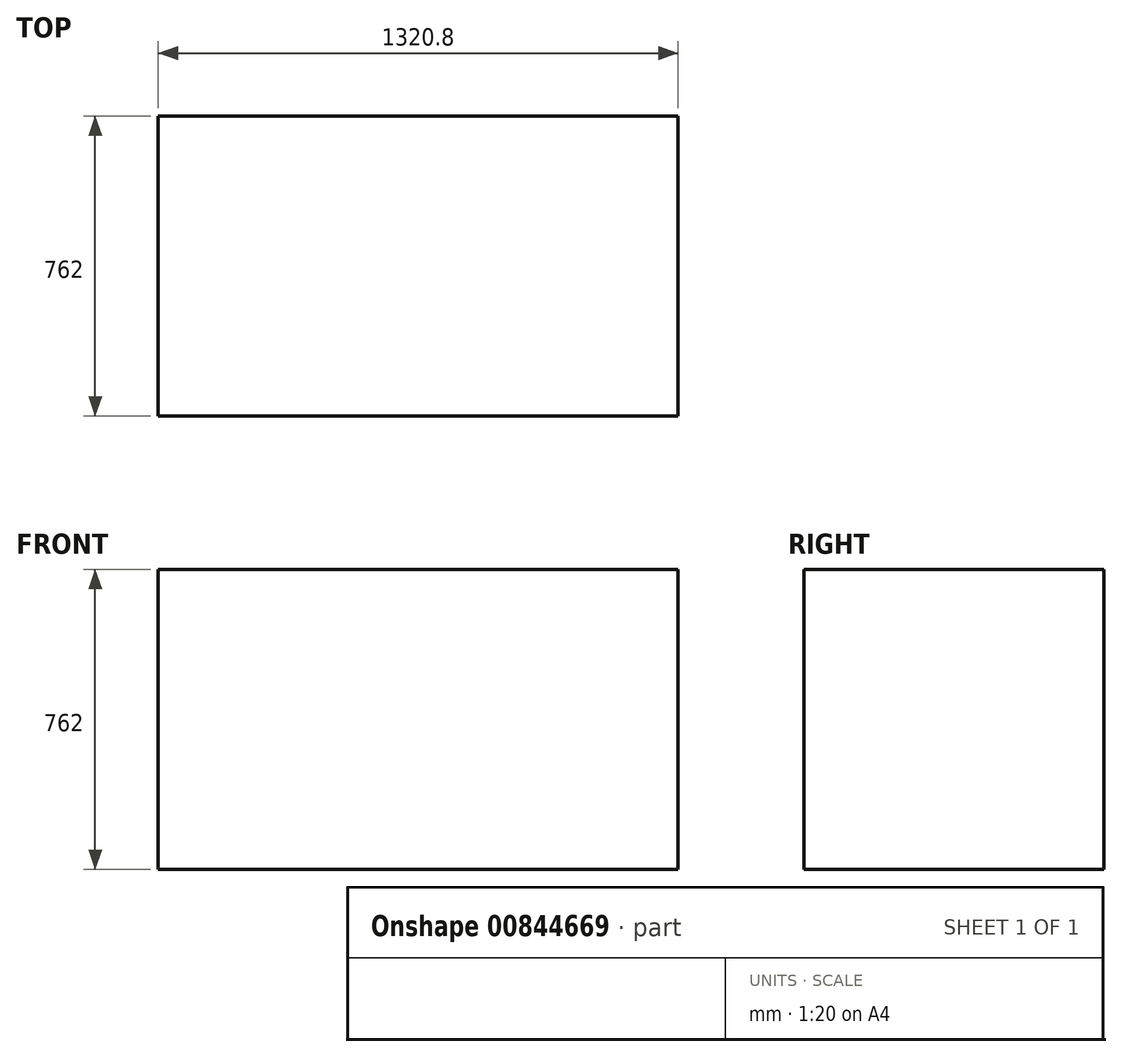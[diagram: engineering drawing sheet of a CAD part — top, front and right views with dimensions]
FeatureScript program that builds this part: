
annotation { "Feature Type Name" : "Feature", "Feature Type Description" : "" }
export const myFeature = defineFeature(function(context is Context, id is Id, definition is map)
    precondition{}
    {
        {
            var Q0;
            Q0=qCreatedBy(makeId("Front.planeOp"),FACE);
            var sketch = newSketch(context, id + "F0", { "sketchPlane" : qUnion([Q0])});
            skLineSegment(sketch, "E0.bottom", {"start": v(660.4, 381) * mm, "end": v(-660.4, 381) * mm});
            skLineSegment(sketch, "E0.top", {"start": v(660.4, -381) * mm, "end": v(-660.4, -381) * mm});
            skLineSegment(sketch, "E0.left", {"start": v(660.4, 381) * mm, "end": v(660.4, -381) * mm});
            skLineSegment(sketch, "E0.right", {"start": v(-660.4, 381) * mm, "end": v(-660.4, -381) * mm});
            skPoint(sketch, "E0.middle", {"position": v(0, 0) * mm});
            skSolve(sketch);
        }
        {
            var Q0;
            Q0 = qSketchRegion(id + "F0", true);
            extrude(context, id + "F1", {"entities" : qUnion([Q0]), "endBound" : BoundingType.SYMMETRIC, "depth" : 762 * mm, "offsetDistance" : 25.4 * mm});
        }
    });
